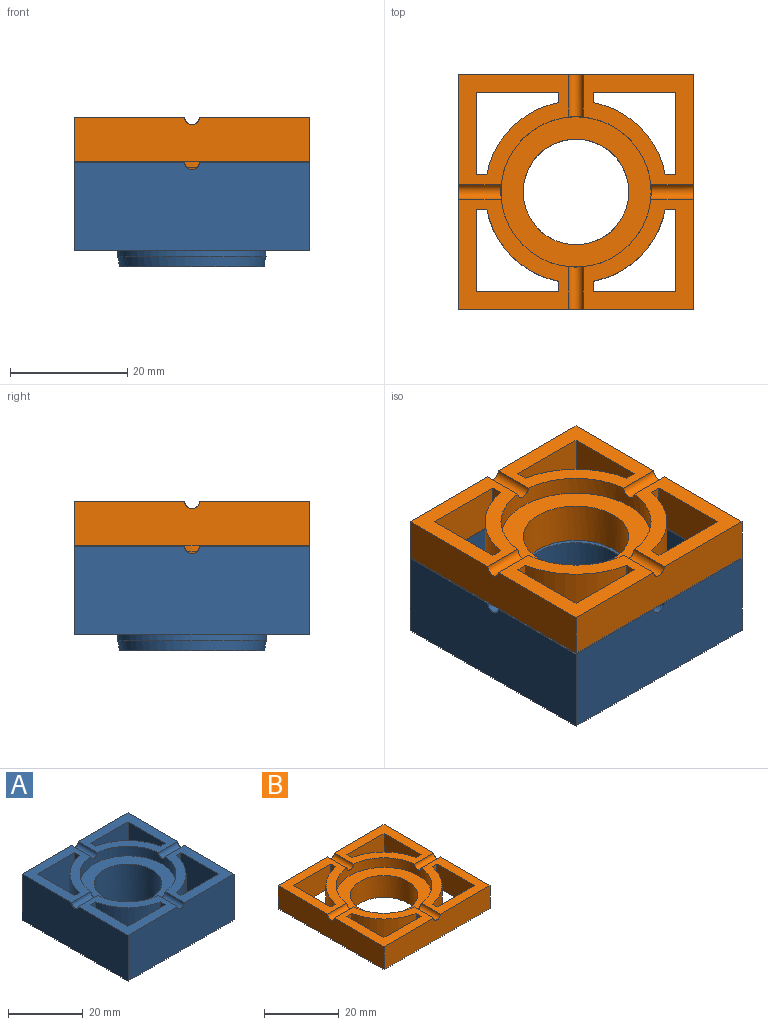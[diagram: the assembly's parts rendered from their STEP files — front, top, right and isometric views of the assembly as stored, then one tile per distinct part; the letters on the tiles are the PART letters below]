
ASSEMBLY  parts=2 mates=1
PART A: 39 faces, bbox 40x40x17.8 mm
  f0: plane 18.75x18.75mm, normal (0,0,1), area 162.5mm2, adj f4,f7,f9,f12,f14,f23,f24,f25
  f1: plane 40x40mm, normal (0,0,-1), area 734.4mm2, adj f4,f5,f6,f7,f15,f18,f19,f20
  f2: plane 18.75x18.75mm, normal (0,0,1), area 162.5mm2, adj f6,f7,f9,f12,f13,f28,f29,f30
  f3: plane 18.75x18.75mm, normal (0,0,1), area 162.5mm2, adj f5,f6,f9,f11,f13,f33,f34,f35
  f4: plane 40x15mm, normal (0,1,0), area 597.5mm2, adj f0,f1,f5,f7,f8,f14
  f5: plane 40x15mm, normal (-1,0,0), area 597.5mm2, adj f1,f3,f4,f6,f8,f11
  f6: plane 40x15mm, normal (0,-1,0), area 597.5mm2, adj f1,f2,f3,f5,f7,f13
  f7: plane 40x15mm, normal (1,0,0), area 597.5mm2, adj f0,f1,f2,f4,f6,f12
  f8: plane 18.75x18.75mm, normal (0,0,1), area 162.5mm2, adj f4,f5,f9,f11,f14,f18,f19,f20
  f9: cylinder r=12.8mm len=25.6mm, axis (0,0,1), area 239.5mm2, adj f0,f2,f3,f8,f10,f11,f12,f13
  f10: plane 25.6x25.6mm, normal (0,0,1), area 260.2mm2, adj f9,f17
  f11: cylinder r=1.25mm len=7.26mm, axis (1,0,0), area 28.4mm2, adj f3,f5,f8,f9
  f12: cylinder r=1.25mm len=7.26mm, axis (1,0,0), area 28.4mm2, adj f0,f2,f7,f9
  f13: cylinder r=1.25mm len=7.26mm, axis (0,1,0), area 28.4mm2, adj f2,f3,f6,f9
  f14: cylinder r=1.25mm len=7.26mm, axis (0,1,0), area 28.4mm2, adj f0,f4,f8,f9
  f15: cylinder r=12.65mm len=25.3mm, axis (0,0,1), area 83.3mm2, adj f1,f38
  f16: plane 24.7x24.7mm, normal (0,0,-1), area 224.7mm2, adj f17,f38
  f17: cylinder r=9mm len=18mm, axis (0,0,-1), area 828.4mm2, adj f10,f16
  f18: plane 15x14mm, normal (0,-1,0), area 210mm2, adj f1,f8,f19,f22
  f19: plane 15x1.79mm, normal (-1,0,0), area 26.9mm2, adj f1,f8,f18,f20
  f20: cylinder r=15.5mm len=15mm, axis (0,0,-1), area 274.6mm2, adj f1,f8,f19,f21
  f21: plane 15x1.79mm, normal (0,1,0), area 26.9mm2, adj f1,f8,f20,f22
  f22: plane 15x14mm, normal (1,0,0), area 210mm2, adj f1,f8,f18,f21
  f23: cylinder r=15.5mm len=15mm, axis (0,0,-1), area 274.6mm2, adj f0,f1,f24,f27
  f24: plane 15x1.79mm, normal (1,0,0), area 26.9mm2, adj f0,f1,f23,f25
  f25: plane 15x14mm, normal (0,-1,0), area 210mm2, adj f0,f1,f24,f26
  f26: plane 15x14mm, normal (-1,0,0), area 210mm2, adj f0,f1,f25,f27
  f27: plane 15x1.79mm, normal (0,1,0), area 26.9mm2, adj f0,f1,f23,f26
  f28: plane 15x14mm, normal (0,1,0), area 210mm2, adj f1,f2,f29,f32
  f29: plane 15x1.79mm, normal (1,0,0), area 26.9mm2, adj f1,f2,f28,f30
  f30: cylinder r=15.5mm len=15mm, axis (0,0,-1), area 274.6mm2, adj f1,f2,f29,f31
  f31: plane 15x1.79mm, normal (0,-1,0), area 26.9mm2, adj f1,f2,f30,f32
  f32: plane 15x14mm, normal (-1,0,0), area 210mm2, adj f1,f2,f28,f31
  f33: plane 15x14mm, normal (1,0,0), area 210mm2, adj f1,f3,f34,f37
  f34: plane 15x1.79mm, normal (0,-1,0), area 26.9mm2, adj f1,f3,f33,f35
  f35: cylinder r=15.5mm len=15mm, axis (0,0,-1), area 274.6mm2, adj f1,f3,f34,f36
  f36: plane 15x1.79mm, normal (-1,0,0), area 26.9mm2, adj f1,f3,f35,f37
  f37: plane 15x14mm, normal (0,1,0), area 210mm2, adj f1,f3,f33,f36
  f38: cone r=12.35mm half-angle=10deg, axis (0,0,1), area 135.7mm2, adj f15,f16
PART B: 39 faces, bbox 40x40x10.3 mm
  f0: plane 18.75x18.75mm, normal (0,0,1), area 162.5mm2, adj f4,f7,f9,f12,f14,f23,f24,f25
  f1: plane 40x40mm, normal (0,0,-1), area 734.4mm2, adj f4,f5,f6,f7,f15,f18,f19,f20
  f2: plane 18.75x18.75mm, normal (0,0,1), area 162.5mm2, adj f6,f7,f9,f12,f13,f28,f29,f30
  f3: plane 18.75x18.75mm, normal (0,0,1), area 162.5mm2, adj f5,f6,f9,f11,f13,f33,f34,f35
  f4: plane 40x7.5mm, normal (0,1,0), area 297.5mm2, adj f0,f1,f5,f7,f8,f14
  f5: plane 40x7.5mm, normal (-1,0,0), area 297.5mm2, adj f1,f3,f4,f6,f8,f11
  f6: plane 40x7.5mm, normal (0,-1,0), area 297.5mm2, adj f1,f2,f3,f5,f7,f13
  f7: plane 40x7.5mm, normal (1,0,0), area 297.5mm2, adj f0,f1,f2,f4,f6,f12
  f8: plane 18.75x18.75mm, normal (0,0,1), area 162.5mm2, adj f4,f5,f9,f11,f14,f18,f19,f20
  f9: cylinder r=12.8mm len=25.6mm, axis (0,0,1), area 239.5mm2, adj f0,f2,f3,f8,f10,f11,f12,f13
  f10: plane 25.6x25.6mm, normal (0,0,1), area 260.2mm2, adj f9,f17
  f11: cylinder r=1.25mm len=7.26mm, axis (1,0,0), area 28.4mm2, adj f3,f5,f8,f9
  f12: cylinder r=1.25mm len=7.26mm, axis (1,0,0), area 28.4mm2, adj f0,f2,f7,f9
  f13: cylinder r=1.25mm len=7.26mm, axis (0,1,0), area 28.4mm2, adj f2,f3,f6,f9
  f14: cylinder r=1.25mm len=7.26mm, axis (0,1,0), area 28.4mm2, adj f0,f4,f8,f9
  f15: cylinder r=12.65mm len=25.3mm, axis (0,0,1), area 83.3mm2, adj f1,f38
  f16: plane 24.7x24.7mm, normal (0,0,-1), area 224.7mm2, adj f17,f38
  f17: cylinder r=9mm len=18mm, axis (0,0,-1), area 404.3mm2, adj f10,f16
  f18: plane 14x7.5mm, normal (0,-1,0), area 105mm2, adj f1,f8,f19,f22
  f19: plane 7.5x1.79mm, normal (-1,0,0), area 13.4mm2, adj f1,f8,f18,f20
  f20: cylinder r=15.5mm len=12.21mm, axis (0,0,-1), area 137.3mm2, adj f1,f8,f19,f21
  f21: plane 7.5x1.79mm, normal (0,1,0), area 13.4mm2, adj f1,f8,f20,f22
  f22: plane 14x7.5mm, normal (1,0,0), area 105mm2, adj f1,f8,f18,f21
  f23: cylinder r=15.5mm len=12.21mm, axis (0,0,-1), area 137.3mm2, adj f0,f1,f24,f27
  f24: plane 7.5x1.79mm, normal (1,0,0), area 13.4mm2, adj f0,f1,f23,f25
  f25: plane 14x7.5mm, normal (0,-1,0), area 105mm2, adj f0,f1,f24,f26
  f26: plane 14x7.5mm, normal (-1,0,0), area 105mm2, adj f0,f1,f25,f27
  f27: plane 7.5x1.79mm, normal (0,1,0), area 13.4mm2, adj f0,f1,f23,f26
  f28: plane 14x7.5mm, normal (0,1,0), area 105mm2, adj f1,f2,f29,f32
  f29: plane 7.5x1.79mm, normal (1,0,0), area 13.4mm2, adj f1,f2,f28,f30
  f30: cylinder r=15.5mm len=12.21mm, axis (0,0,-1), area 137.3mm2, adj f1,f2,f29,f31
  f31: plane 7.5x1.79mm, normal (0,-1,0), area 13.4mm2, adj f1,f2,f30,f32
  f32: plane 14x7.5mm, normal (-1,0,0), area 105mm2, adj f1,f2,f28,f31
  f33: plane 14x7.5mm, normal (1,0,0), area 105mm2, adj f1,f3,f34,f37
  f34: plane 7.5x1.79mm, normal (0,-1,0), area 13.4mm2, adj f1,f3,f33,f35
  f35: cylinder r=15.5mm len=12.21mm, axis (0,0,-1), area 137.3mm2, adj f1,f3,f34,f36
  f36: plane 7.5x1.79mm, normal (-1,0,0), area 13.4mm2, adj f1,f3,f35,f37
  f37: plane 14x7.5mm, normal (0,1,0), area 105mm2, adj f1,f3,f33,f36
  f38: cone r=12.35mm half-angle=10deg, axis (0,0,1), area 135.7mm2, adj f15,f16
PLACE A t=(-26.61,19.98,2.36)mm
PLACE B t=(-26.61,19.98,17.51)mm
MATE slider A.f9 <-> B.f9  axis (0,0,-1) through (-6.61,-0.02,14.26)mm
